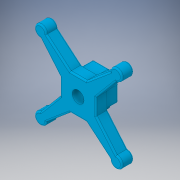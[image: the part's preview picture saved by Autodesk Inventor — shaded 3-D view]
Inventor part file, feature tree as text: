
AUTODESK INVENTOR PART (.ipt)
format: ipt  version: 2019 (Build 230136000, 136)  size: 327,680 bytes
history: native  units: in
note: dims shown in document units (in); Inventor stores cm internally (conversion verified against a paired STEP export)
features: sketch x4, fillet x3, extrude x2, pattern_circular x1
ambient origin geometry x8: Origin, YZ Plane, XZ Plane, XY Plane, X Axis, Y Axis, Z Axis, Center Point
bodies: Solid1 (feature_tree)
feature tree (10):
  extrude  "Extrusion1"  Depth=0.125in
  fillet  "Fillet1"  Radius=0.125in
  sketch  "Sketch2"  dims[d4=0.6875in d5=3.0in]
  fillet  "Fillet2"  Radius=1.0in
  sketch  "Sketch3"  dims[d6=0.6875in]
  sketch  "Sketch4"  dims[d7=1.0in d8=1.5748in d10=360.0deg d12=1.0in d13=0.0in d14=0.125in d15=0.125in d16=0.75in d17=1.0in d18=0.0in d19=1.5748in d20=360.0deg d22=0.125in]
  extrude  "Extrusion2"  Depth=3.0in
  pattern_circular  "Circular Pattern1"  Count=4 Angle=360.0deg
  fillet  "Fillet3"  Radius=1.0in
  sketch  "Sketch1"  dims[d0=3.0in d1=3.0in d2=0.125in d3=1.0in]
